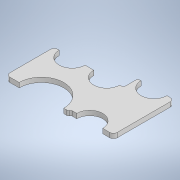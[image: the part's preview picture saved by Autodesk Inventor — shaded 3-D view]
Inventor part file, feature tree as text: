
AUTODESK INVENTOR PART (.ipt)
format: ipt  version: 2021 (Build 250183000, 183)  size: 190,464 bytes
history: native  units: mm
features: extrude x3, sketch x3, projected_geometry x2, fillet x1
ambient origin geometry x8: Origin, YZ Plane, XZ Plane, XY Plane, X Axis, Y Axis, Z Axis, Center Point
bodies: Solid1 (feature_tree)
feature tree (9):
  extrude  "Extrusion1"  Depth=56.25mm
  sketch  "Sketch2"  dims[d16=58.25mm d17=116.5mm]
  extrude  "Extrusion2"  Depth=116.5mm
  extrude  "Extrusion3"  Depth=4.0mm
  fillet  "Fillet1"  Radius=32.45mm
  sketch  "Sketch1"  dims[d0=47.7mm d1=27.7mm d2=27.7mm d3=27.7mm d4=27.7mm d7=37.0mm d9=30.9mm d10=19.5mm d11=35.0mm d12=35.0mm d13=25.8mm d14=28.0mm d15=56.25mm]
  projected_geometry  "Projected Loop1"
  sketch  "Sketch3"  dims[d18=112.5mm d19=18.5mm d20=32.45mm d21=5.0mm d22=0.0mm d23=74.0mm d25=38.5mm d26=2.0mm d27=35.0mm d28=19.5mm d29=67.0mm d30=2.0mm d31=10.0mm d32=0.0mm d33=0.0mm d34=0.0mm d35=4.0mm]
  projected_geometry  "Projected Loop2"
